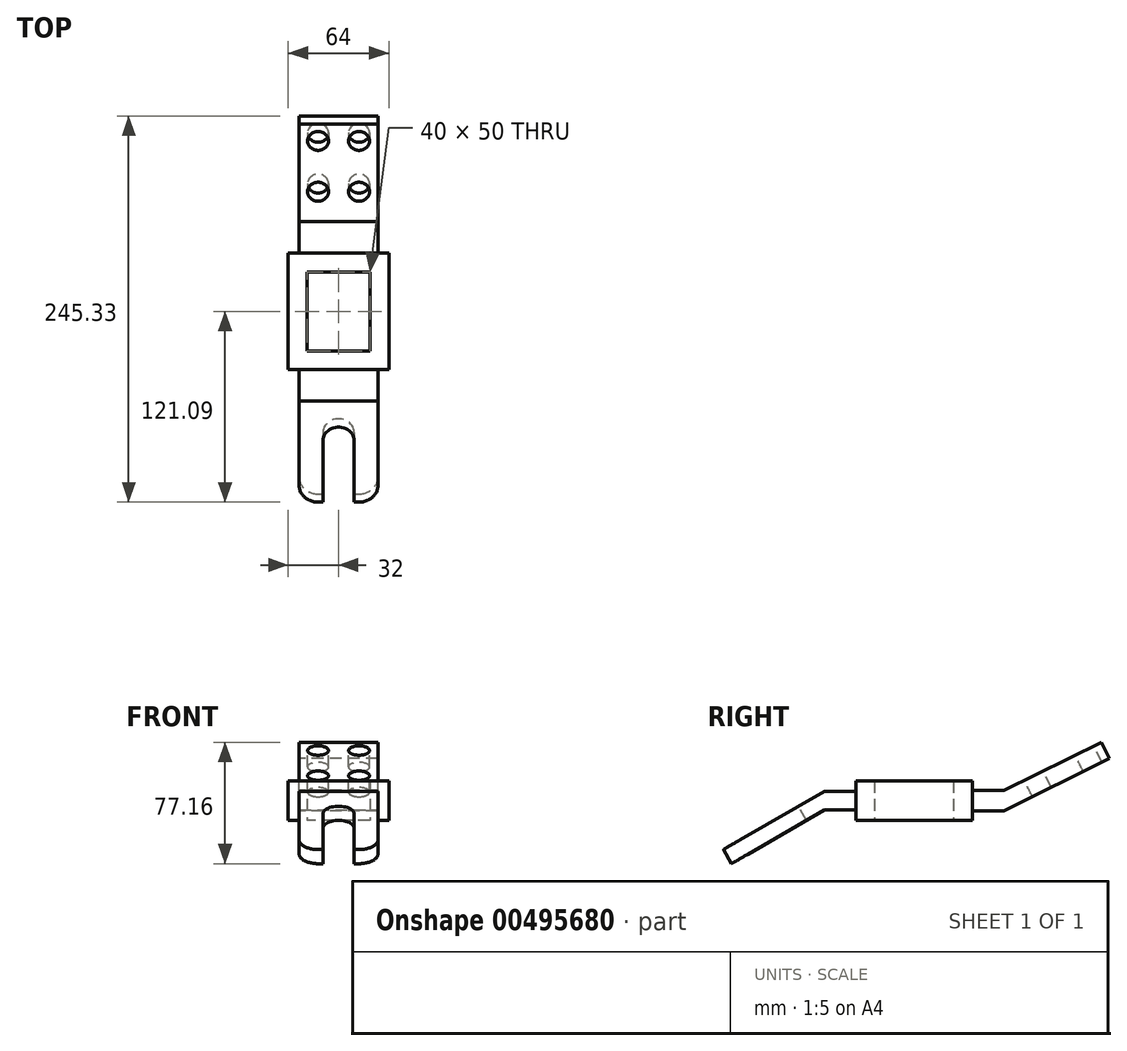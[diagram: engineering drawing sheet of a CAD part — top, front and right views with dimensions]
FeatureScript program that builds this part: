
annotation { "Feature Type Name" : "Feature", "Feature Type Description" : "" }
export const myFeature = defineFeature(function(context is Context, id is Id, definition is map)
    precondition{}
    {
        {
            var Q0;
            Q0=qCreatedBy(makeId("Top.planeOp"),FACE);
            var sketch = newSketch(context, id + "F0", { "sketchPlane" : qUnion([Q0])});
            skLineSegment(sketch, "E0.bottom", {"start": v(32, 37) * mm, "end": v(-32, 37) * mm});
            skLineSegment(sketch, "E0.top", {"start": v(32, -37) * mm, "end": v(-32, -37) * mm});
            skLineSegment(sketch, "E0.left", {"start": v(32, 37) * mm, "end": v(32, -37) * mm});
            skLineSegment(sketch, "E0.right", {"start": v(-32, 37) * mm, "end": v(-32, -37) * mm});
            skPoint(sketch, "E0.middle", {"position": v(0, 0) * mm});
            skLineSegment(sketch, "E1.bottom", {"start": v(20, 25) * mm, "end": v(-20, 25) * mm});
            skLineSegment(sketch, "E1.top", {"start": v(20, -25) * mm, "end": v(-20, -25) * mm});
            skLineSegment(sketch, "E1.left", {"start": v(20, 25) * mm, "end": v(20, -25) * mm});
            skLineSegment(sketch, "E1.right", {"start": v(-20, 25) * mm, "end": v(-20, -25) * mm});
            skSolve(sketch);
        }
        {
            var Q0;
            Q0 = qSketchRegion(id + "F0", true);
            extrude(context, id + "F1", {"entities" : qUnion([Q0]), "depth" : 25 * mm});
        }
        {
            var Q0;
            Q0=qCreatedBy(makeId("Right.planeOp"),FACE);
            var sketch = newSketch(context, id + "F2", { "sketchPlane" : qUnion([Q0])});
            skLineSegment(sketch, "E2.0", {"start": v(-37, 25) * mm, "end": v(-37, 0) * mm});
            skLineSegment(sketch, "E3", {"start": v(-37, 12.5) * mm, "end": v(-37, 18.5) * mm});
            skLineSegment(sketch, "E4", {"start": v(-37, 18.5) * mm, "end": v(-37, 12.5) * mm});
            skLineSegment(sketch, "E5", {"start": v(-37, 12.5) * mm, "end": v(-37, 6.5) * mm});
            skLineSegment(sketch, "E6", {"start": v(-37, 18.5) * mm, "end": v(-57, 18.5) * mm});
            skLineSegment(sketch, "E7", {"start": v(-57, 18.5) * mm, "end": v(-57, 6.5) * mm});
            skLineSegment(sketch, "E8", {"start": v(-57, 6.5) * mm, "end": v(-37, 6.5) * mm});
            skLineSegment(sketch, "E9", {"start": v(-57, 18.5) * mm, "end": v(-88.13, 18.5) * mm});
            skLineSegment(sketch, "E10", {"start": v(-57, 18.5) * mm, "end": v(-121.09, -18.5) * mm});
            skLineSegment(sketch, "E11", {"start": v(-57, 6.5) * mm, "end": v(-121.09, -30.5) * mm});
            skLineSegment(sketch, "E12", {"start": v(-121.09, -18.5) * mm, "end": v(-115.89, -27.5) * mm});
            skSolve(sketch);
        }
        {
            var Q0;
            Q0 = qSketchRegion(id + "F2", true);
            extrude(context, id + "F3", {"entities" : qUnion([Q0]), "operationType" : NewBodyOperationType.ADD, "oppositeDirection" : true, "depth" : 25 * mm, "hasSecondDirection" : true, "secondDirectionOppositeDirection" : false, "secondDirectionDepth" : 25 * mm});
        }
        {
            var Q0;
            Q0=makeQuery(id+"F3.opExtrude","SWEPT_FACE",FACE,{"disambiguationData":[OSD([sQuery(id+"F2.wireOp",EDGE,"E10")])]});
            var sketch = newSketch(context, id + "F4", { "sketchPlane" : qUnion([Q0])});
            skLineSegment(sketch, "E13", {"start": v(-25, -114.11) * mm, "end": v(0, -114.11) * mm});
            skLineSegment(sketch, "E14", {"start": v(0, -114.11) * mm, "end": v(25, -114.11) * mm});
            skLineSegment(sketch, "E15", {"start": v(0, -114.11) * mm, "end": v(0, -69.11) * mm});
            skCircle(sketch, "E16", {"center": v(0, -69.11) * mm, "radius": 10 * mm});
            skLineSegment(sketch, "E17", {"start": v(-10, -69.11) * mm, "end": v(-10, -114.11) * mm});
            skLineSegment(sketch, "E18", {"start": v(10, -69.11) * mm, "end": v(10, -114.11) * mm});
            skSolve(sketch);
        }
        {
            var Q0;
            {var subQ3=sQuery(id+"F4.wireOp",EDGE,"E18");Q0=makeQuery(id+"F4.imprint","IMPRINT",FACE,{"disambiguationData":[TD([[makeQuery(id+"F4.imprint","IMPRINT",EDGE,{"derivedFrom":subQ3}),-1.0]])]});}
            var Q1;
            {var subQ0=sQuery(id+"F4.wireOp",EDGE,"E16");var subQ1=makeQuery(id+"F4.imprint","INTERSECT",VERTEX,{"derivedFrom":[subQ0,sQuery(id+"F4.wireOp",EDGE,"E17")]});Q1=makeQuery(id+"F4.imprint","IMPRINT",FACE,{"disambiguationData":[TD([[makeQuery(id+"F4.imprint","IMPRINT",EDGE,{"disambiguationData":[TD([[subQ1,1.0]])],"derivedFrom":subQ0}),1.0]])]});}
            var Q2;
            {var subQ3=sQuery(id+"F4.wireOp",EDGE,"E17");Q2=makeQuery(id+"F4.imprint","IMPRINT",FACE,{"disambiguationData":[TD([[makeQuery(id+"F4.imprint","IMPRINT",EDGE,{"derivedFrom":subQ3}),1.0]])]});}
            extrude(context, id + "F5", {"entities" : qUnion([Q0, Q1, Q2]), "operationType" : NewBodyOperationType.REMOVE, "oppositeDirection" : true, "depth" : 25 * mm});
        }
        {
            var Q0;
            Q0=makeQuery(id+"F3.opExtrude","CAP_EDGE",EDGE,{"disambiguationData":[OSD([sQuery(id+"F2.wireOp",EDGE,"E12")])],"isStart":false});
            fillet(context, id + "F6", {"entities" : qUnion([Q0]), "radius" : 12 * mm, "tangentPropagation" : true, "allowEdgeOverflow" : false});
        }
        {
            var Q0;
            Q0=makeQuery(id+"F3.opExtrude","CAP_EDGE",EDGE,{"disambiguationData":[OSD([sQuery(id+"F2.wireOp",EDGE,"E12")])],"isStart":true});
            fillet(context, id + "F7", {"entities" : qUnion([Q0]), "radius" : 12 * mm, "tangentPropagation" : true, "allowEdgeOverflow" : false});
        }
        {
            var Q0;
            Q0=qCreatedBy(makeId("Right.planeOp"),FACE);
            var sketch = newSketch(context, id + "F8", { "sketchPlane" : qUnion([Q0])});
            skPoint(sketch, "E19.0", {"position": v(37, 12.5) * mm});
            skLineSegment(sketch, "E20.0", {"start": v(37, 25) * mm, "end": v(37, 0) * mm});
            skLineSegment(sketch, "E21", {"start": v(57, 19) * mm, "end": v(37, 19) * mm});
            skLineSegment(sketch, "E22", {"start": v(37, 0) * mm, "end": v(37, 6) * mm});
            skLineSegment(sketch, "E23", {"start": v(37, 6) * mm, "end": v(57, 6) * mm});
            skLineSegment(sketch, "E24", {"start": v(57, 6) * mm, "end": v(149.43, 0) * mm});
            skLineSegment(sketch, "E25", {"start": v(57, 19) * mm, "end": v(119.08, 49.66) * mm});
            skLineSegment(sketch, "E26", {"start": v(57, 6) * mm, "end": v(124.24, 39.21) * mm});
            skLineSegment(sketch, "E27", {"start": v(124.24, 39.21) * mm, "end": v(119.08, 49.66) * mm});
            skSolve(sketch);
        }
        {
            var Q0;
            Q0 = qSketchRegion(id + "F8", true);
            extrude(context, id + "F9", {"entities" : qUnion([Q0]), "operationType" : NewBodyOperationType.ADD, "depth" : 25 * mm, "hasSecondDirection" : true, "secondDirectionOppositeDirection" : true, "secondDirectionDepth" : 25 * mm});
        }
        {
            var Q0;
            Q0=makeQuery(id+"F9.opExtrude","SWEPT_FACE",FACE,{"disambiguationData":[OSD([sQuery(id+"F8.wireOp",EDGE,"E25")])]});
            var sketch = newSketch(context, id + "F10", { "sketchPlane" : qUnion([Q0])});
            skLineSegment(sketch, "E28", {"start": v(-25, 128.76) * mm, "end": v(-13, 128.76) * mm});
            skLineSegment(sketch, "E29", {"start": v(25, 128.76) * mm, "end": v(13, 128.76) * mm});
            skLineSegment(sketch, "E30", {"start": v(13, 128.76) * mm, "end": v(-13, 128.76) * mm});
            skLineSegment(sketch, "E31", {"start": v(-25, 128.76) * mm, "end": v(-25, 116.76) * mm});
            skLineSegment(sketch, "E32", {"start": v(-25, 116.76) * mm, "end": v(25, 116.76) * mm});
            skCircle(sketch, "E33", {"center": v(-13, 116.76) * mm, "radius": 6.7 * mm});
            skCircle(sketch, "E34", {"center": v(13, 116.76) * mm, "radius": 6.7 * mm});
            skLineSegment(sketch, "E35", {"start": v(-25, 116.76) * mm, "end": v(-25, 80.76) * mm});
            skLineSegment(sketch, "E36", {"start": v(-25, 80.76) * mm, "end": v(25, 80.76) * mm});
            skCircle(sketch, "E37", {"center": v(-13, 80.76) * mm, "radius": 6.7 * mm});
            skCircle(sketch, "E38", {"center": v(13, 80.76) * mm, "radius": 6.7 * mm});
            skSolve(sketch);
        }
        {
            var Q0;
            Q0 = qSketchRegion(id + "F10", true);
            extrude(context, id + "F11", {"entities" : qUnion([Q0]), "operationType" : NewBodyOperationType.REMOVE, "oppositeDirection" : true, "depth" : 25 * mm});
        }
    });
